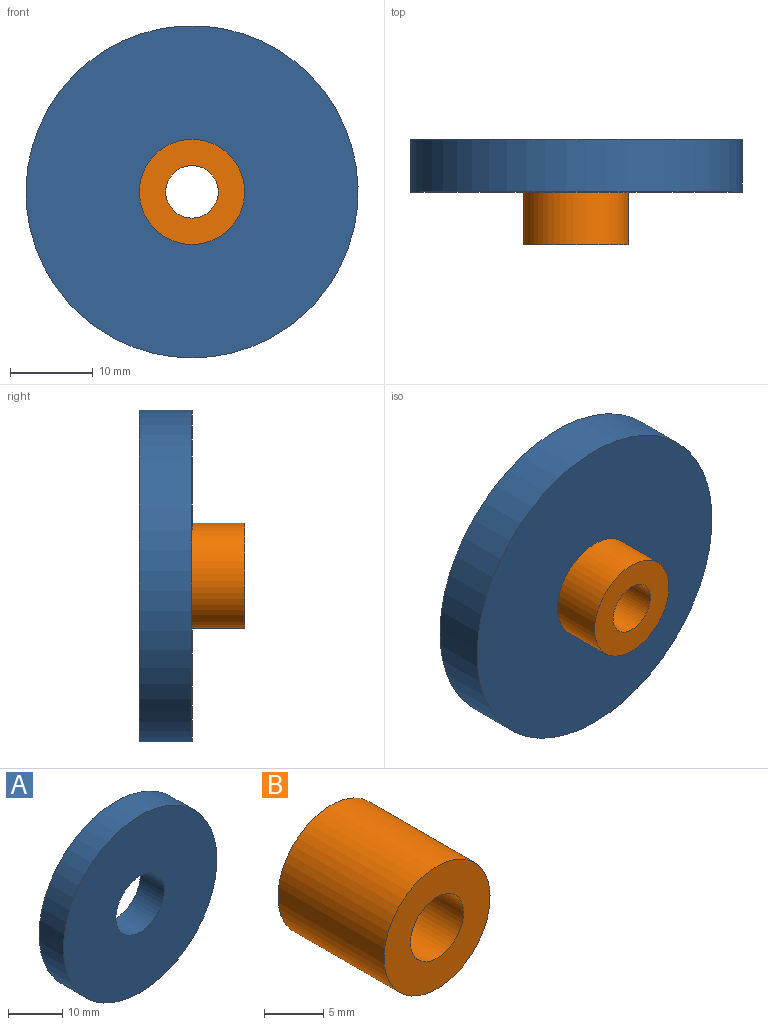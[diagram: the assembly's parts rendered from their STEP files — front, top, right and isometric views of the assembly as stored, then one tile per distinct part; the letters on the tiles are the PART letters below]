
ASSEMBLY  parts=2 mates=1
PART A: 4 faces, bbox 40.1x6.4x40.1 mm
  f0: cylinder r=20.07mm len=40.13mm, axis (0,-1,0), area 800.6mm2, adj f1,f3
  f1: plane 40.13x40.13mm, normal (0,-1,0), area 1138.3mm2, adj f0,f2
  f2: cylinder r=6.35mm len=12.7mm, axis (0,-1,0), area 253.4mm2, adj f1,f3
  f3: plane 40.13x40.13mm, normal (0,1,0), area 1138.3mm2, adj f0,f2
PART B: 4 faces, bbox 12.7x12.7x12.7 mm
  f0: plane 12.7x12.7mm, normal (0,-1,0), area 95mm2, adj f1,f3
  f1: cylinder r=3.17mm len=12.7mm, axis (0,-1,0), area 253.4mm2, adj f0,f2
  f2: plane 12.7x12.7mm, normal (0,1,0), area 95mm2, adj f1,f3
  f3: cylinder r=6.35mm len=12.7mm, axis (0,-1,0), area 506.7mm2, adj f0,f2
PLACE A t=(0,9.52,0)mm
PLACE B t=(0,4.76,0)mm
MATE fastened B.f1 <-> A.f0  axis (0,1,0) through (0,12.7,0)mm
